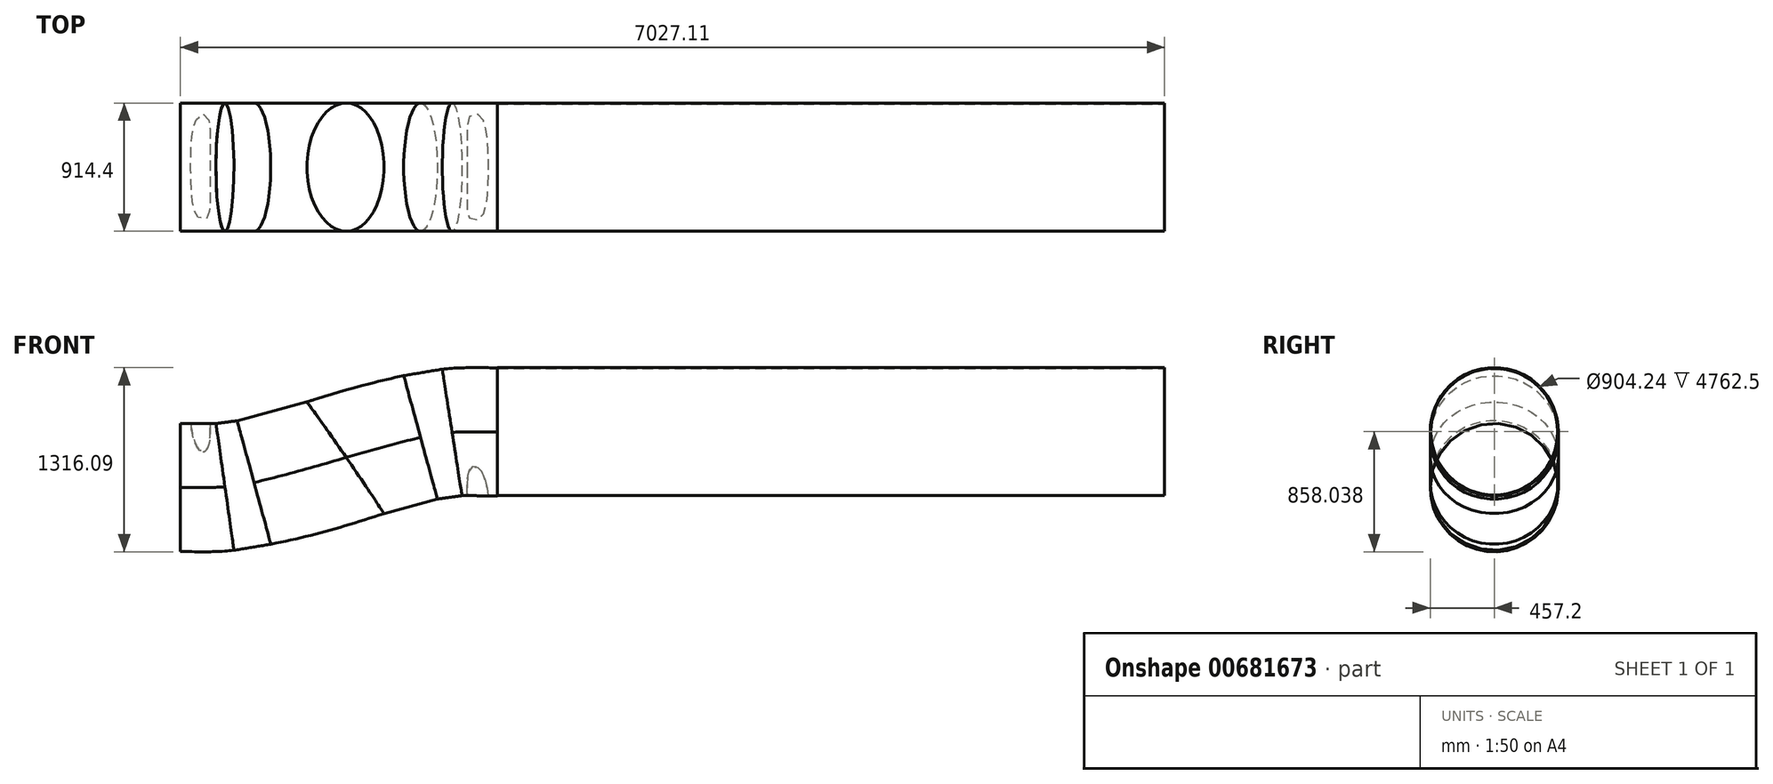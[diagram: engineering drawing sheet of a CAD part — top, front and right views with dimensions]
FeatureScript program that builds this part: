
annotation { "Feature Type Name" : "Feature", "Feature Type Description" : "" }
export const myFeature = defineFeature(function(context is Context, id is Id, definition is map)
    precondition{}
    {
        {
            var Q0;
            Q0=qCreatedBy(makeId("Right.planeOp"),FACE);
            var sketch = newSketch(context, id + "F0", { "sketchPlane" : qUnion([Q0])});
            skCircle(sketch, "E0", {"center": v(0, 0) * mm, "radius": 457.2 * mm});
            skSolve(sketch);
        }
        {
            var Q0;
            Q0=qCreatedBy(makeId("Front.planeOp"),FACE);
            var sketch = newSketch(context, id + "F1", { "sketchPlane" : qUnion([Q0])});
            skLineSegment(sketch, "E1", {"start": v(317.5, 0) * mm, "end": v(0, 0) * mm});
            skLineSegment(sketch, "E2", {"start": v(317.5, 0) * mm, "end": v(517.84, 33.98) * mm});
            skLineSegment(sketch, "E3", {"start": v(317.5, 0) * mm, "end": v(1939.35, 275.12) * mm});
            skLineSegment(sketch, "E4", {"start": v(0, 456.47) * mm, "end": v(254, 456.47) * mm});
            skLineSegment(sketch, "E5", {"start": v(0, -441.83) * mm, "end": v(381, -441.83) * mm});
            skLineSegment(sketch, "E6", {"start": v(254, 456.47) * mm, "end": v(381, -441.83) * mm});
            skLineSegment(sketch, "E7", {"start": v(254, 456.47) * mm, "end": v(404.9, 477.8) * mm});
            skLineSegment(sketch, "E8", {"start": v(381, -441.83) * mm, "end": v(645.07, -404.5) * mm});
            skLineSegment(sketch, "E9", {"start": v(645.07, -404.5) * mm, "end": v(404.9, 477.8) * mm});
            skLineSegment(sketch, "E10", {"start": v(404.9, 477.8) * mm, "end": v(1593.55, 801.37) * mm});
            skLineSegment(sketch, "E11", {"start": v(645.07, -404.5) * mm, "end": v(1833.72, -80.92) * mm});
            skLineSegment(sketch, "E12", {"start": v(1593.55, 801.37) * mm, "end": v(1833.72, -80.92) * mm});
            skLineSegment(sketch, "E13", {"start": v(517.84, 33.98) * mm, "end": v(1713.82, 359.55) * mm});
            skLineSegment(sketch, "E14", {"start": v(1593.55, 801.37) * mm, "end": v(1869.01, 848.1) * mm});
            skLineSegment(sketch, "E15", {"start": v(1869.01, 848.1) * mm, "end": v(2009.68, -55.41) * mm});
            skLineSegment(sketch, "E16", {"start": v(2009.68, -55.41) * mm, "end": v(1833.72, -80.92) * mm});
            skPoint(sketch, "E17.endSnap0", {"position": v(1939.35, 396.34) * mm});
            skLineSegment(sketch, "E18", {"start": v(1939.35, 396.34) * mm, "end": v(1713.82, 359.55) * mm});
            skLineSegment(sketch, "E19", {"start": v(1869.01, 848.1) * mm, "end": v(2264.61, 848.1) * mm});
            skLineSegment(sketch, "E20", {"start": v(2009.68, -55.41) * mm, "end": v(2263.68, -55.41) * mm});
            skLineSegment(sketch, "E21", {"start": v(2263.68, -55.41) * mm, "end": v(2263.68, 848.1) * mm});
            skLineSegment(sketch, "E22", {"start": v(1939.35, 396.34) * mm, "end": v(2263.68, 396.34) * mm});
            skLineSegment(sketch, "E23", {"start": v(2264.61, 848.1) * mm, "end": v(7027.11, 848.1) * mm});
            skLineSegment(sketch, "E24", {"start": v(2263.68, 396.34) * mm, "end": v(7026.18, 396.34) * mm});
            skLineSegment(sketch, "E25", {"start": v(7027.11, 848.1) * mm, "end": v(7027.11, -66.3) * mm});
            skSolve(sketch);
        }
        {
            var Q0;
            Q0=sQuery(id+"F1.wireOp",EDGE,"E6");
            cPlane(context, id + "F2", {"entities" : qUnion([Q0]), "cplaneType" : CPlaneType.LINE_ANGLE, "offset" : 25.4 * mm, "angle" : 0 * degree, "width" : 152.4 * mm, "height" : 152.4 * mm});
        }
        {
            var Q0;
            Q0=sQuery(id+"F1.wireOp",EDGE,"E9");
            cPlane(context, id + "F3", {"entities" : qUnion([Q0]), "cplaneType" : CPlaneType.LINE_ANGLE, "offset" : 25.4 * mm, "angle" : 0 * degree, "width" : 152.4 * mm, "height" : 152.4 * mm});
        }
        {
            var Q0;
            Q0=sQuery(id+"F1.wireOp",EDGE,"E12");
            cPlane(context, id + "F4", {"entities" : qUnion([Q0]), "cplaneType" : CPlaneType.LINE_ANGLE, "offset" : 25.4 * mm, "angle" : 0 * degree, "width" : 152.4 * mm, "height" : 152.4 * mm});
        }
        {
            var Q0;
            Q0=sQuery(id+"F1.wireOp",EDGE,"E15");
            cPlane(context, id + "F5", {"entities" : qUnion([Q0]), "cplaneType" : CPlaneType.LINE_ANGLE, "offset" : 25.4 * mm, "angle" : 0 * degree, "width" : 152.4 * mm, "height" : 152.4 * mm});
        }
        {
            var Q0;
            Q0=sQuery(id+"F1.wireOp",EDGE,"E21");
            cPlane(context, id + "F6", {"entities" : qUnion([Q0]), "cplaneType" : CPlaneType.LINE_ANGLE, "offset" : 25.4 * mm, "angle" : 0 * degree, "width" : 152.4 * mm, "height" : 152.4 * mm});
        }
        {
            var Q0;
            Q0=sQuery(id+"F1.wireOp",EDGE,"E25");
            cPlane(context, id + "F7", {"entities" : qUnion([Q0]), "cplaneType" : CPlaneType.LINE_ANGLE, "offset" : 25.4 * mm, "angle" : 0 * degree, "width" : 152.4 * mm, "height" : 152.4 * mm});
        }
        {
            var Q0;
            Q0=qCreatedBy(id+"F2.planeOp",FACE);
            var sketch = newSketch(context, id + "F8", { "sketchPlane" : qUnion([Q0])});
            skCircle(sketch, "E26", {"center": v(0, -41.5) * mm, "radius": 457.2 * mm});
            skSolve(sketch);
        }
        {
            var Q0;
            Q0=qCreatedBy(id+"F3.planeOp",FACE);
            var sketch = newSketch(context, id + "F9", { "sketchPlane" : qUnion([Q0])});
            skCircle(sketch, "E27", {"center": v(0, -104.3) * mm, "radius": 457.2 * mm});
            skSolve(sketch);
        }
        {
            var Q0;
            Q0=qCreatedBy(id+"F4.planeOp",FACE);
            var sketch = newSketch(context, id + "F10", { "sketchPlane" : qUnion([Q0])});
            skCircle(sketch, "E28", {"center": v(0, -105.89) * mm, "radius": 457.2 * mm});
            skSolve(sketch);
        }
        {
            var Q0;
            Q0=qCreatedBy(id+"F5.planeOp",FACE);
            var sketch = newSketch(context, id + "F11", { "sketchPlane" : qUnion([Q0])});
            skCircle(sketch, "E29", {"center": v(0, 89.86) * mm, "radius": 457.2 * mm});
            skSolve(sketch);
        }
        {
            var Q0;
            Q0=qCreatedBy(id+"F6.planeOp",FACE);
            var sketch = newSketch(context, id + "F12", { "sketchPlane" : qUnion([Q0])});
            skCircle(sketch, "E30", {"center": v(0, 396.1) * mm, "radius": 457.2 * mm});
            skSolve(sketch);
        }
        {
            var Q0;
            Q0=makeQuery(id+"F0.imprint","IMPRINT",FACE,{"disambiguationData":[TD([[makeQuery(id+"F0.imprint","IMPRINT",EDGE,{"derivedFrom":sQuery(id+"F0.wireOp",EDGE,"E0")}),1.0]])]});
            var Q1;
            Q1=makeQuery(id+"F8.imprint","IMPRINT",FACE,{"disambiguationData":[TD([[makeQuery(id+"F8.imprint","IMPRINT",EDGE,{"derivedFrom":sQuery(id+"F8.wireOp",EDGE,"E26")}),1.0]])]});
            loft(context, id + "F13", {"sheetProfilesArray" : [{ "sheetProfileEntities" : qUnion([Q0]) }, { "sheetProfileEntities" : qUnion([Q1]) }]});
        }
        {
            var Q1;
            Q1=makeQuery(id+"F13.opLoft","CAP_FACE",FACE,{"disambiguationData":[OSD([makeQuery(id+"F8.imprint","IMPRINT",FACE,{"disambiguationData":[TD([[makeQuery(id+"F8.imprint","IMPRINT",EDGE,{"derivedFrom":sQuery(id+"F8.wireOp",EDGE,"E26")}),1.0]])]})])],"isStart":true});
            var Q2;
            Q2=makeQuery(id+"F9.imprint","IMPRINT",FACE,{"disambiguationData":[TD([[makeQuery(id+"F9.imprint","IMPRINT",EDGE,{"derivedFrom":sQuery(id+"F9.wireOp",EDGE,"E27")}),1.0]])]});
            loft(context, id + "F14", {"operationType" : NewBodyOperationType.ADD, "sheetProfilesArray" : [{ "sheetProfileEntities" : qUnion([Q1]) }, { "sheetProfileEntities" : qUnion([Q2]) }]});
        }
        {
            var Q0;
            Q0=makeQuery(id+"F14.opLoft","CAP_FACE",FACE,{"disambiguationData":[OSD([makeQuery(id+"F9.imprint","IMPRINT",FACE,{"disambiguationData":[TD([[makeQuery(id+"F9.imprint","IMPRINT",EDGE,{"derivedFrom":sQuery(id+"F9.wireOp",EDGE,"E27")}),1.0]])]})])],"isStart":true});
            var Q1;
            Q1=makeQuery(id+"F10.imprint","IMPRINT",FACE,{"disambiguationData":[TD([[makeQuery(id+"F10.imprint","IMPRINT",EDGE,{"derivedFrom":sQuery(id+"F10.wireOp",EDGE,"E28")}),1.0]])]});
            loft(context, id + "F15", {"sheetProfilesArray" : [{ "sheetProfileEntities" : qUnion([Q0]) }, { "sheetProfileEntities" : qUnion([Q1]) }]});
        }
        {
            var Q1;
            Q1=makeQuery(id+"F15.opLoft","CAP_FACE",FACE,{"disambiguationData":[OSD([makeQuery(id+"F10.imprint","IMPRINT",FACE,{"disambiguationData":[TD([[makeQuery(id+"F10.imprint","IMPRINT",EDGE,{"derivedFrom":sQuery(id+"F10.wireOp",EDGE,"E28")}),1.0]])]})])],"isStart":true});
            var Q2;
            Q2=makeQuery(id+"F11.imprint","IMPRINT",FACE,{"disambiguationData":[TD([[makeQuery(id+"F11.imprint","IMPRINT",EDGE,{"derivedFrom":sQuery(id+"F11.wireOp",EDGE,"E29")}),1.0]])]});
            loft(context, id + "F16", {"operationType" : NewBodyOperationType.ADD, "sheetProfilesArray" : [{ "sheetProfileEntities" : qUnion([Q1]) }, { "sheetProfileEntities" : qUnion([Q2]) }]});
        }
        {
            var Q0;
            Q0=makeQuery(id+"F16.opLoft","CAP_FACE",FACE,{"disambiguationData":[OSD([makeQuery(id+"F11.imprint","IMPRINT",FACE,{"disambiguationData":[TD([[makeQuery(id+"F11.imprint","IMPRINT",EDGE,{"derivedFrom":sQuery(id+"F11.wireOp",EDGE,"E29")}),1.0]])]})])],"isStart":true});
            var Q1;
            Q1=makeQuery(id+"F12.imprint","IMPRINT",FACE,{"disambiguationData":[TD([[makeQuery(id+"F12.imprint","IMPRINT",EDGE,{"derivedFrom":sQuery(id+"F12.wireOp",EDGE,"E30")}),1.0]])]});
            loft(context, id + "F17", {"sheetProfilesArray" : [{ "sheetProfileEntities" : qUnion([Q0]) }, { "sheetProfileEntities" : qUnion([Q1]) }]});
        }
        {
            var Q0;
            Q0=makeQuery(id+"F17.opLoft","CAP_FACE",FACE,{"disambiguationData":[OSD([makeQuery(id+"F12.imprint","IMPRINT",FACE,{"disambiguationData":[TD([[makeQuery(id+"F12.imprint","IMPRINT",EDGE,{"derivedFrom":sQuery(id+"F12.wireOp",EDGE,"E30")}),1.0]])]})])],"isStart":true});
            var Q1;
            Q1=makeQuery(id+"F13.opLoft","CAP_FACE",FACE,{"disambiguationData":[OSD([makeQuery(id+"F0.imprint","IMPRINT",FACE,{"disambiguationData":[TD([[makeQuery(id+"F0.imprint","IMPRINT",EDGE,{"derivedFrom":sQuery(id+"F0.wireOp",EDGE,"E0")}),1.0]])]})])],"isStart":true});
            shell(context, id + "F18", {"entities" : qUnion([Q0, Q1]), "thickness" : 2.54 * mm});
        }
        {
            var Q0;
            Q0=qCreatedBy(id+"F7.planeOp",FACE);
            var sketch = newSketch(context, id + "F19", { "sketchPlane" : qUnion([Q0])});
            skCircle(sketch, "E31", {"center": v(0, 397.48) * mm, "radius": 457.2 * mm});
            skSolve(sketch);
        }
        {
            var Q0;
            Q0=makeQuery(id+"F19.imprint","IMPRINT",FACE,{"disambiguationData":[TD([[makeQuery(id+"F19.imprint","IMPRINT",EDGE,{"derivedFrom":sQuery(id+"F19.wireOp",EDGE,"E31")}),1.0]])]});
            extrude(context, id + "F20", {"entities" : qUnion([Q0]), "depth" : 4762.5 * mm, "offsetDistance" : 25.4 * mm});
        }
        {
            var Q0;
            Q0=makeQuery(id+"F20.opExtrude","CAP_FACE",FACE,{"disambiguationData":[OSD([sQuery(id+"F19.wireOp",EDGE,"E31")])],"isStart":true});
            var Q1;
            Q1=makeQuery(id+"F20.opExtrude","CAP_FACE",FACE,{"disambiguationData":[OSD([sQuery(id+"F19.wireOp",EDGE,"E31")])],"isStart":false});
            shell(context, id + "F21", {"entities" : qUnion([Q0, Q1]), "thickness" : 5.08 * mm});
        }
        {
            var Q0;
            Q0=makeQuery(id+"F14.opLoft","CAP_FACE",FACE,{"disambiguationData":[OSD([makeQuery(id+"F9.imprint","IMPRINT",FACE,{"disambiguationData":[TD([[makeQuery(id+"F9.imprint","IMPRINT",EDGE,{"derivedFrom":sQuery(id+"F9.wireOp",EDGE,"E27")}),1.0]])]})])],"isStart":true});
            var Q1;
            Q1=makeQuery(id+"F10.imprint","IMPRINT",FACE,{"disambiguationData":[TD([[makeQuery(id+"F10.imprint","IMPRINT",EDGE,{"derivedFrom":sQuery(id+"F10.wireOp",EDGE,"E28")}),1.0]])]});
            loft(context, id + "F22", {"operationType" : NewBodyOperationType.ADD, "sheetProfilesArray" : [{ "sheetProfileEntities" : qUnion([Q0]) }, { "sheetProfileEntities" : qUnion([Q1]) }]});
        }
        {
            var Q0;
            Q0=makeQuery(id+"F0.imprint","IMPRINT",FACE,{"disambiguationData":[TD([[makeQuery(id+"F0.imprint","IMPRINT",EDGE,{"derivedFrom":sQuery(id+"F0.wireOp",EDGE,"E0")}),1.0]])]});
            var Q1;
            Q1=makeQuery(id+"F8.imprint","IMPRINT",FACE,{"disambiguationData":[TD([[makeQuery(id+"F8.imprint","IMPRINT",EDGE,{"derivedFrom":sQuery(id+"F8.wireOp",EDGE,"E26")}),1.0]])]});
            var Q2;
            Q2=makeQuery(id+"F9.imprint","IMPRINT",FACE,{"disambiguationData":[TD([[makeQuery(id+"F9.imprint","IMPRINT",EDGE,{"derivedFrom":sQuery(id+"F9.wireOp",EDGE,"E27")}),1.0]])]});
            var Q3;
            Q3=makeQuery(id+"F10.imprint","IMPRINT",FACE,{"disambiguationData":[TD([[makeQuery(id+"F10.imprint","IMPRINT",EDGE,{"derivedFrom":sQuery(id+"F10.wireOp",EDGE,"E28")}),1.0]])]});
            var Q4;
            Q4=makeQuery(id+"F11.imprint","IMPRINT",FACE,{"disambiguationData":[TD([[makeQuery(id+"F11.imprint","IMPRINT",EDGE,{"derivedFrom":sQuery(id+"F11.wireOp",EDGE,"E29")}),1.0]])]});
            var Q5;
            Q5=makeQuery(id+"F12.imprint","IMPRINT",FACE,{"disambiguationData":[TD([[makeQuery(id+"F12.imprint","IMPRINT",EDGE,{"derivedFrom":sQuery(id+"F12.wireOp",EDGE,"E30")}),1.0]])]});
            loft(context, id + "F23", {"operationType" : NewBodyOperationType.ADD, "sheetProfilesArray" : [{ "sheetProfileEntities" : qUnion([Q0]) }, { "sheetProfileEntities" : qUnion([Q1]) }, { "sheetProfileEntities" : qUnion([Q2]) }, { "sheetProfileEntities" : qUnion([Q3]) }, { "sheetProfileEntities" : qUnion([Q4]) }, { "sheetProfileEntities" : qUnion([Q5]) }]});
        }
    });
